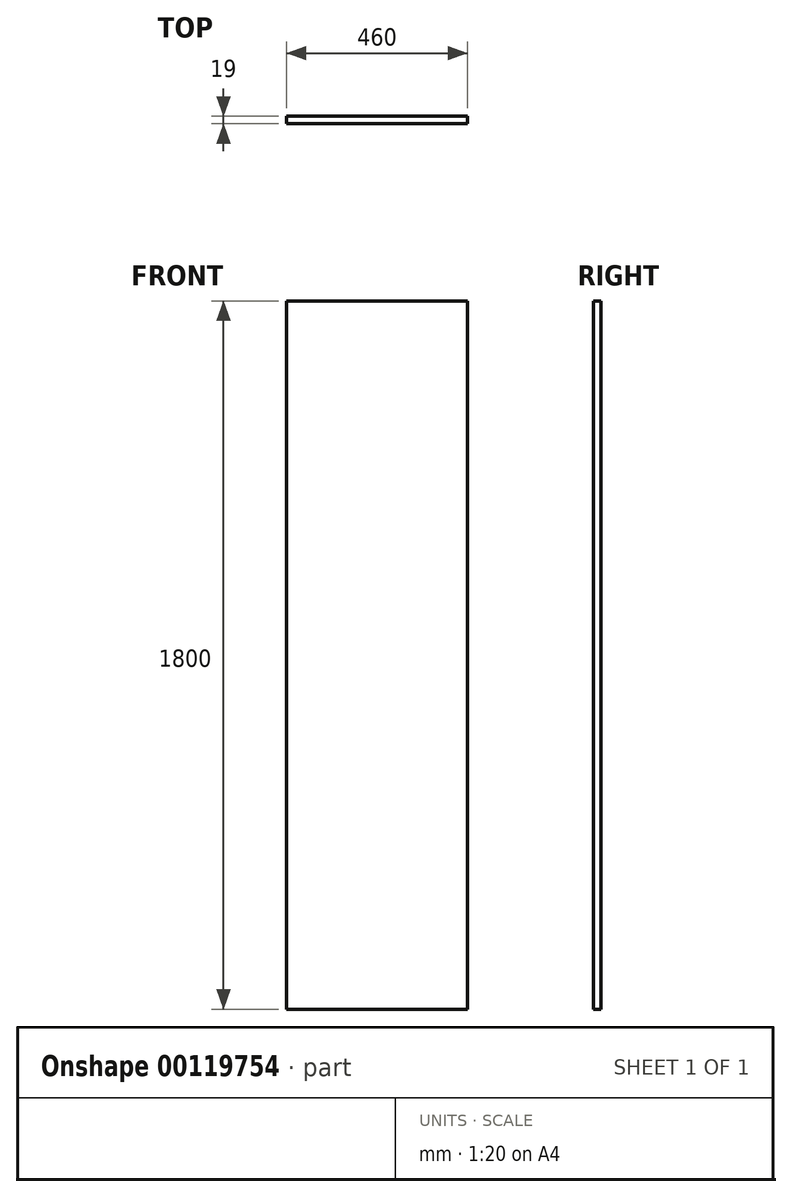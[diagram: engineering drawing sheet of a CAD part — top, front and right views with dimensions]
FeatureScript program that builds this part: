
annotation { "Feature Type Name" : "Feature", "Feature Type Description" : "" }
export const myFeature = defineFeature(function(context is Context, id is Id, definition is map)
    precondition{}
    {
        {
            var Q0;
            Q0=qCreatedBy(makeId("Front.planeOp"),FACE);
            var sketch = newSketch(context, id + "F0", { "sketchPlane" : qUnion([Q0])});
            skLineSegment(sketch, "E0.bottom", {"start": v(-230, 900) * mm, "end": v(230, 900) * mm});
            skLineSegment(sketch, "E0.top", {"start": v(-230, -900) * mm, "end": v(230, -900) * mm});
            skLineSegment(sketch, "E0.left", {"start": v(-230, 900) * mm, "end": v(-230, -900) * mm});
            skLineSegment(sketch, "E0.right", {"start": v(230, 900) * mm, "end": v(230, -900) * mm});
            skPoint(sketch, "E0.middle", {"position": v(0, 0) * mm});
            skSolve(sketch);
        }
        {
            var Q0;
            Q0=makeQuery(id+"F0.imprint","IMPRINT",FACE,{"disambiguationData":[TD([[makeQuery(id+"F0.imprint","IMPRINT",EDGE,{"derivedFrom":sQuery(id+"F0.wireOp",EDGE,"E0.bottom")}),-1.0]])]});
            extrude(context, id + "F1", {"entities" : qUnion([Q0]), "depth" : 19 * mm});
        }
    });
